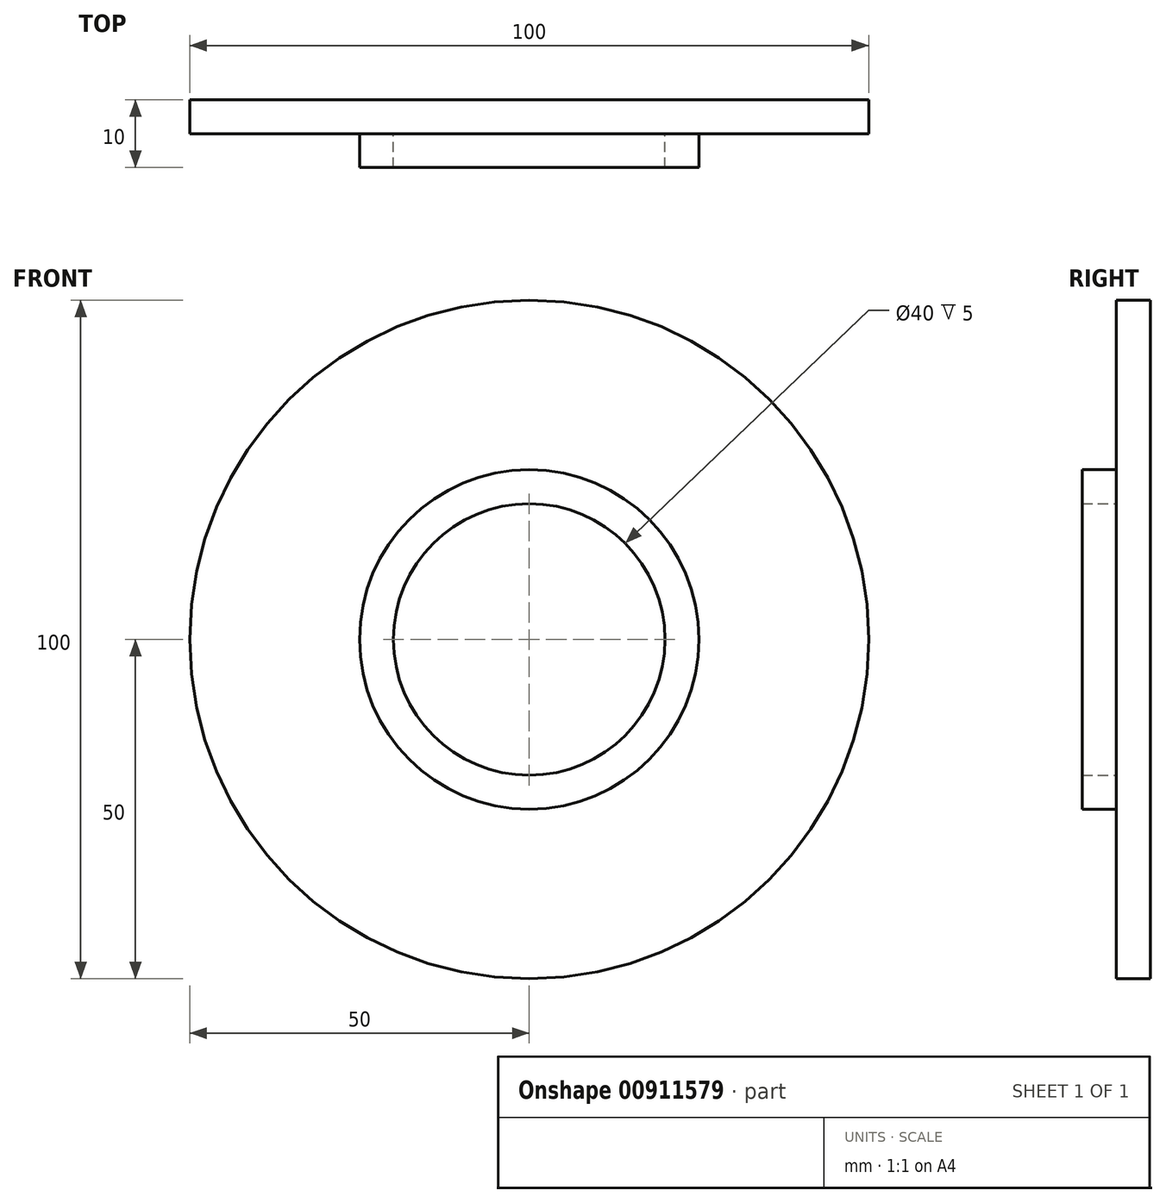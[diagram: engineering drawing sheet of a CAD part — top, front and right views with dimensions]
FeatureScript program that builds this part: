
annotation { "Feature Type Name" : "Feature", "Feature Type Description" : "" }
export const myFeature = defineFeature(function(context is Context, id is Id, definition is map)
    precondition{}
    {
        {
            var Q0;
            Q0=qCreatedBy(makeId("Front.planeOp"),FACE);
            var sketch = newSketch(context, id + "F0", { "sketchPlane" : qUnion([Q0])});
            skCircle(sketch, "E0", {"center": v(0, 0) * mm, "radius": 50 * mm});
            skCircle(sketch, "E1", {"center": v(0, 0) * mm, "radius": 20 * mm});
            skCircle(sketch, "E2", {"center": v(0, 0) * mm, "radius": 25 * mm});
            skSolve(sketch);
        }
        {
            var Q0;
            Q0 = qSketchRegion(id + "F0", true);
            var Q1;
            Q1=makeQuery(id+"F0.imprint","IMPRINT",FACE,{"disambiguationData":[TD([[makeQuery(id+"F0.imprint","IMPRINT",EDGE,{"derivedFrom":sQuery(id+"F0.wireOp",EDGE,"E1")}),-1.0]])]});
            var Q2;
            Q2=makeQuery(id+"F0.imprint","IMPRINT",FACE,{"disambiguationData":[TD([[makeQuery(id+"F0.imprint","IMPRINT",EDGE,{"derivedFrom":sQuery(id+"F0.wireOp",EDGE,"E1")}),1.0]])]});
            extrude(context, id + "F1", {"entities" : qUnion([Q0, Q1, Q2]), "depth" : 5 * mm, "offsetDistance" : 25 * mm});
        }
        {
            var Q0;
            Q0=makeQuery(id+"F0.imprint","IMPRINT",FACE,{"disambiguationData":[TD([[makeQuery(id+"F0.imprint","IMPRINT",EDGE,{"derivedFrom":sQuery(id+"F0.wireOp",EDGE,"E1")}),-1.0]])]});
            extrude(context, id + "F2", {"entities" : qUnion([Q0]), "operationType" : NewBodyOperationType.ADD, "depth" : 10 * mm, "offsetDistance" : 25 * mm});
        }
    });
